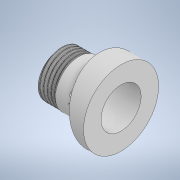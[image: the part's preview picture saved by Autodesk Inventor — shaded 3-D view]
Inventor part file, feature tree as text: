
AUTODESK INVENTOR PART (.ipt)
format: ipt  version: 2021.1 (Build 251245010, 245A)  size: 792,064 bytes
history: native  units: in
note: dims shown in document units (in); Inventor stores cm internally (conversion verified against a paired STEP export)
features: sketch x4, plane x3, revolve x1, helix x1, emboss x1, extrude x1
ambient origin geometry x8: Origin, YZ Plane, XZ Plane, XY Plane, X Axis, Y Axis, Z Axis, Center Point
bodies: Solid1 (feature_tree)
feature tree (11):
  revolve  "Revolution1"  [1 undecoded]
  helix  "Coil1"  [1 undecoded]
  plane  "Work Plane2"
  emboss  "Emboss2"
  plane  "Work Plane4"
  extrude  "Extrusion1"  TaperAngle=90.0deg  [1 undecoded]
  sketch  "Sketch2"  dims[d0=1.0in d1=0.5344in d2=0.125in]
  sketch  "Sketch4"  dims[d3=1.25in d4=90.0deg]
  sketch  "Sketch6"  dims[d5=0.625in]
  plane  "Work Plane3"
  sketch  "Sketch8"  dims[d6=0.25in d10=60.0deg d11=0.0072in d12=60.0deg d13=60.0deg d15=0.1in d16=0.2in d17=0.05in d18=0.6144in d19=0.5494in d20=30.0deg d21=0.1in d22=0.625in d23=0.3937in d24=0.0in d25=90.0deg d26=90.0deg d27=0.0in d28=0.0in d38=0.0906in d39=0.5494in d40=0.6144in d41=0.25in d42=0.05in d43=0.0in d44=0.0825in d45=0.35in d46=1.0in d47=0.0in]
note: 3 required parameter values undecoded (feature->parameter linkage not recoverable at this tier; creation-order binding heuristic only, values carry confidence <= 0.55)